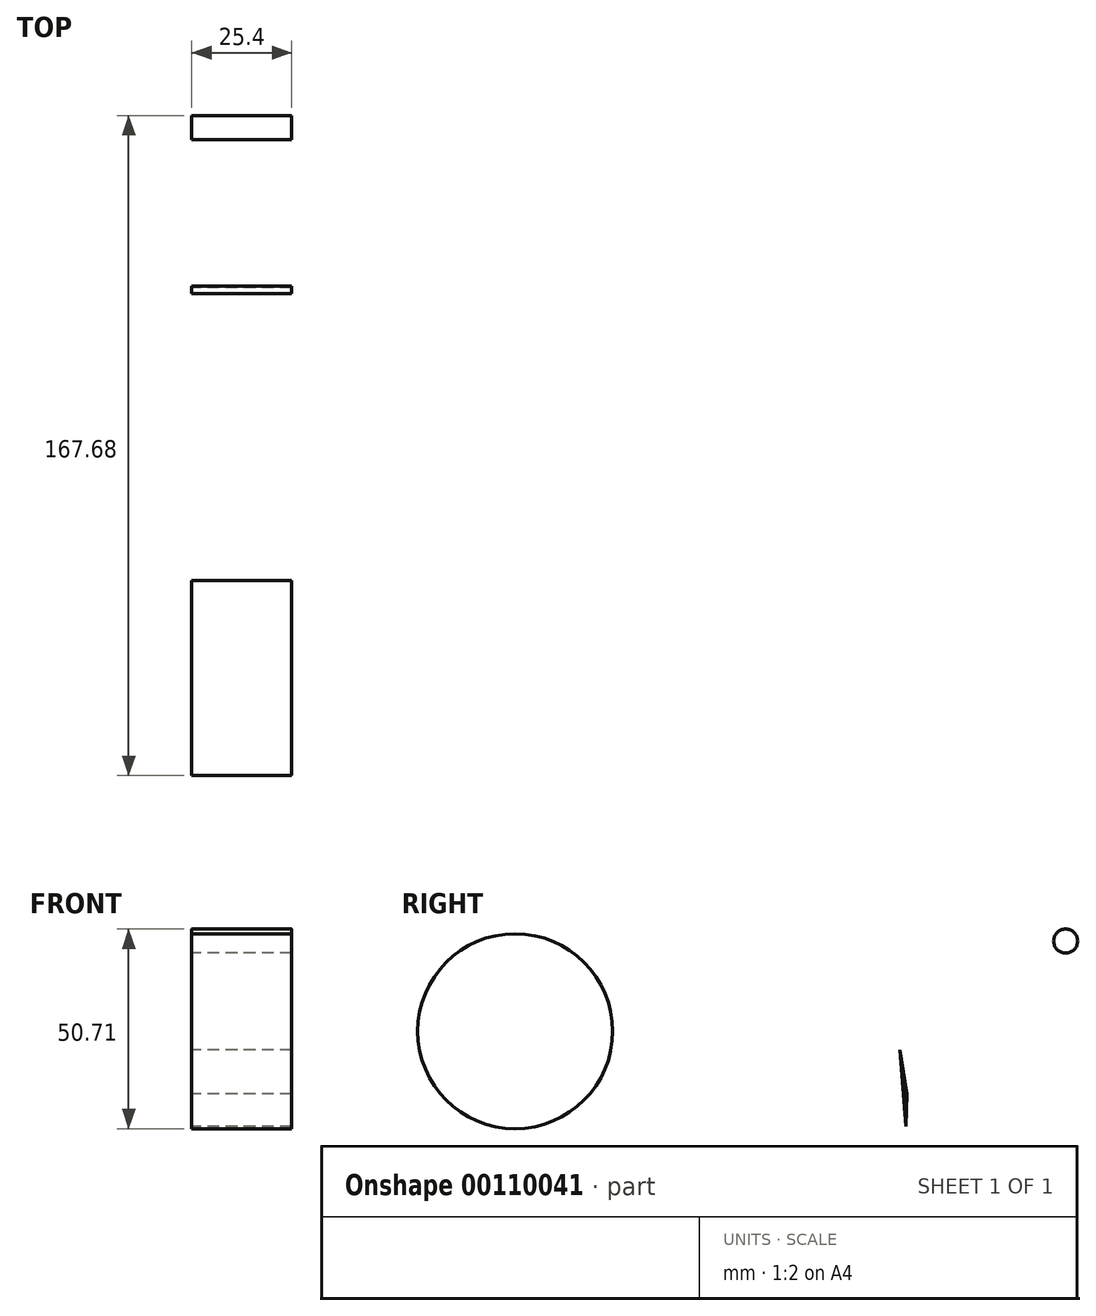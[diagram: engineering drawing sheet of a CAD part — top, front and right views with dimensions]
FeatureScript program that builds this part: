
annotation { "Feature Type Name" : "Feature", "Feature Type Description" : "" }
export const myFeature = defineFeature(function(context is Context, id is Id, definition is map)
    precondition{}
    {
        {
            var Q0;
            Q0=qCreatedBy(makeId("Right.planeOp"),FACE);
            var sketch = newSketch(context, id + "F0", { "sketchPlane" : qUnion([Q0])});
            skCircle(sketch, "E0", {"center": v(-102.66, 33.09) * mm, "radius": 24.76 * mm});
            skLineSegment(sketch, "E1", {"start": v(-70.47, 16.87) * mm, "end": v(-70.47, 54.19) * mm});
            skLineSegment(sketch, "E2", {"start": v(-70.47, 54.19) * mm, "end": v(-47.94, 19.02) * mm});
            skLineSegment(sketch, "E3", {"start": v(-47.94, 19.02) * mm, "end": v(-23.6, 54.55) * mm});
            skLineSegment(sketch, "E4", {"start": v(-23.6, 54.55) * mm, "end": v(-16.15, 11.35) * mm});
            skLineSegment(sketch, "E5", {"start": v(-12.52, 48.82) * mm, "end": v(-9.3, 8.4) * mm});
            skLineSegment(sketch, "E6", {"start": v(-11.95, 41.63) * mm, "end": v(19.2, 44.11) * mm});
            skLineSegment(sketch, "E7", {"start": v(19.2, 44.11) * mm, "end": v(19.2, 37.02) * mm});
            skLineSegment(sketch, "E8", {"start": v(37.93, 45.18) * mm, "end": v(37.93, 3.04) * mm});
            skCircle(sketch, "E9", {"center": v(37.2, 55.98) * mm, "radius": 3.06 * mm});
            skLineSegment(sketch, "E10", {"start": v(-70.47, 16.87) * mm, "end": v(-65.05, 16.87) * mm});
            skLineSegment(sketch, "E11", {"start": v(-65.05, 16.87) * mm, "end": v(-65.05, 41.57) * mm});
            skLineSegment(sketch, "E12", {"start": v(-65.05, 39.66) * mm, "end": v(-48.11, 13.23) * mm});
            skLineSegment(sketch, "E13", {"start": v(-48.11, 13.23) * mm, "end": v(-25.18, 42.05) * mm});
            skLineSegment(sketch, "E14", {"start": v(-25.18, 42.05) * mm, "end": v(-25.18, 10.76) * mm});
            skLineSegment(sketch, "E15", {"start": v(-25.18, 10.76) * mm, "end": v(-18.07, 10.76) * mm});
            skLineSegment(sketch, "E16", {"start": v(-18.07, 10.76) * mm, "end": v(-16.15, 10.76) * mm});
            skLineSegment(sketch, "E17", {"start": v(-16.01, 11.23) * mm, "end": v(-16.15, 10.76) * mm});
            skLineSegment(sketch, "E18", {"start": v(-9.3, 8.4) * mm, "end": v(-3.4, 8.88) * mm});
            skLineSegment(sketch, "E19", {"start": v(-3.4, 8.88) * mm, "end": v(-5.7, 37.73) * mm});
            skLineSegment(sketch, "E20", {"start": v(-5.5, 35.3) * mm, "end": v(-5.7, 37.73) * mm});
            skLineSegment(sketch, "E21", {"start": v(-5.5, 35.3) * mm, "end": v(-4.95, 28.32) * mm});
            skLineSegment(sketch, "E22", {"start": v(-4.95, 28.32) * mm, "end": v(-3.1, 17.2) * mm});
            skLineSegment(sketch, "E23", {"start": v(-3.1, 17.2) * mm, "end": v(-3.4, 8.88) * mm});
            skLineSegment(sketch, "E24", {"start": v(-2.79, 10.84) * mm, "end": v(-5.98, 30.27) * mm});
            skSolve(sketch);
        }
        {
            var Q0;
            Q0 = qSketchRegion(id + "F0", true);
            extrude(context, id + "F1", {"entities" : qUnion([Q0]), "depth" : 25.4 * mm});
        }
    });
